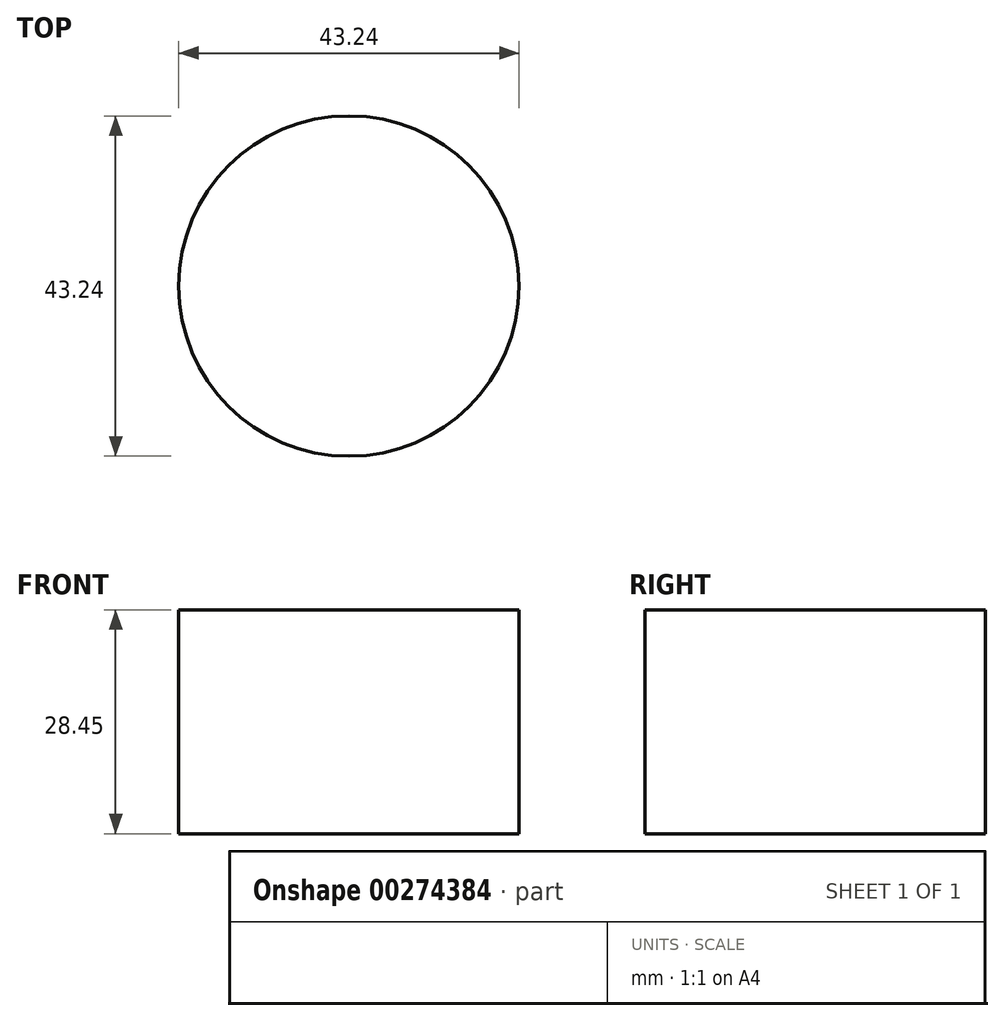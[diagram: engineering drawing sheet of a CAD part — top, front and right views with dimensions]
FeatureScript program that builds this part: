
annotation { "Feature Type Name" : "Feature", "Feature Type Description" : "" }
export const myFeature = defineFeature(function(context is Context, id is Id, definition is map)
    precondition{}
    {
        {
            var Q0;
            Q0=qCreatedBy(makeId("Top.planeOp"),FACE);
            var sketch = newSketch(context, id + "F0", { "sketchPlane" : qUnion([Q0])});
            skCircle(sketch, "E0", {"center": v(-26.46, 40.84) * mm, "radius": 21.62 * mm});
            skPoint(sketch, "E0.first.point", {"position": v(-47.74, 44.68) * mm});
            skPoint(sketch, "E0.second.point", {"position": v(-7.45, 30.55) * mm});
            skPoint(sketch, "E0.third.point", {"position": v(-33.04, 20.24) * mm});
            skSolve(sketch);
        }
        {
            var Q0;
            Q0 = qSketchRegion(id + "F0", true);
            extrude(context, id + "F1", {"entities" : qUnion([Q0]), "depth" : 28.45 * mm});
        }
    });
